# Revit family: Hager-Golf-IP40-Transparent_Door-sistema-NoHosted-IT-it
name_source: partatom
category: Electrical Equipment
units: mm (PartAtom-declared; Revit-internal decimal feet)

## family parameters
Always vertical = Yes
Cut with Voids When Loaded = No
Panel Configuration = Two Columns, Circuits Across
Part Type = Panelboard
Room Calculation Point = No
Round Connector Dimension = Use Diameter
Shared = No
Work Plane-Based = Yes

## types (22) — shared parameters
Default Elevation = 1219 mm
EF000007 - colore = EV000202 - bianco
EF000116 - numero RAL = 9010
EF000118 - con piastra di montaggio = No
EF000339 - tipo di copertura = EV004216 - porta
EF001062 - esecuzione EMC = No
EF001088 - possibilità di applicazione = Yes
EF001134 - barra DIN = Yes
EF001596 - Attacco Lampada = EV000139 - plastica
EF004462 - tipo di chiusura = EV000154 - altri
EF006244 - coperchio/porta trasparente = Yes
EF006306 - con serratura = No
EF009212 - esecuzione coperchio = EV000116 - chiuso
EF015776 - Morsettiera di terra = No
EF015777 - Morsettiera neutra = No
EF015941 - Segnale di passaggio porta = Yes
HG000001 - Numero di colonne = 1
HG000002 - Con porta = Yes
HG000003 - Gamma = Golf
HG000005 - Spessore = 3 mm  [stored 0.00984252 ft]
HG000009 - Porta doppia a battente = No
HG000010 - Porte asimmetriche = No
HG000011 - File vuote nella parte basse = No
HG000017 - Distanza tra i poli = 18 mm  [stored 0.0590551 ft]
Manufacturer = Hager
Type Comments = Golf
zero-valued in all types: HG000007 - Numero di colonne vuote, HG000008 - Numero di file vuote

## per-type parameters (varying)
| type | EF000003 - Tipo di montaggio | EF000008 - Larghezza | EF000040 - Altezza | EF000049 - profondità | EF000218 - profondità di incasso | EF000266 - numero di file | EF000332 - Altezza della parte incassata | EF000846 - larghezza di montaggio | EF001131 - profondità interna | EF002950 - Numero moduli DIN | EF005474 - grado di protezione (IP) | HG000004 - Codice produttore | HG000006 - Ad incasso | Model |
| A parete  L138 A184 P99 4 Unità di divisione - VS104TG | EV000384 - A parete | 138 mm  [stored 0.452756 ft] | 184 mm  [stored 0.603675 ft] | 99 mm  [stored 0.324803 ft] | 0 mm  [stored 0 ft] | 1 | 0 mm  [stored 0 ft] | 0 mm  [stored 0 ft] | 99 mm  [stored 0.324803 ft] | 4 |  | VS104TG | No | VS104TG |
| A parete  L210 A184 P99 8 Unità di divisione - VS108TG | EV000384 - A parete | 210 mm  [stored 0.688976 ft] | 184 mm  [stored 0.603675 ft] | 99 mm  [stored 0.324803 ft] | 0 mm  [stored 0 ft] | 1 | 0 mm  [stored 0 ft] | 0 mm  [stored 0 ft] | 99 mm  [stored 0.324803 ft] | 8 |  | VS108TG | No | VS108TG |
| A parete IP40 L282 A252 P99 12 Unità di divisione - VS112TG | EV000384 - A parete | 282 mm | 252 mm  [stored 0.826772 ft] | 99 mm  [stored 0.324803 ft] | 0 mm  [stored 0 ft] | 1 | 0 mm  [stored 0 ft] | 0 mm  [stored 0 ft] | 99 mm  [stored 0.324803 ft] | 12 | EV006415 - IP40 | VS112TG | No | VS112TG |
| A parete IP40 L282 A377 P99 12 Unità di divisione - VS212TG | EV000384 - A parete | 282 mm | 377 mm  [stored 1.23688 ft] | 99 mm  [stored 0.324803 ft] | 0 mm  [stored 0 ft] | 2 | 0 mm  [stored 0 ft] | 0 mm  [stored 0 ft] | 99 mm  [stored 0.324803 ft] | 12 | EV006415 - IP40 | VS212TG | No | VS212TG |
| A parete IP40 L282 A500 P99 12 Unità di divisione - VS312TG | EV000384 - A parete | 282 mm | 500 mm  [stored 1.64042 ft] | 99 mm  [stored 0.324803 ft] | 0 mm  [stored 0 ft] | 3 | 0 mm  [stored 0 ft] | 0 mm  [stored 0 ft] | 99 mm  [stored 0.324803 ft] | 12 | EV006415 - IP40 | VS312TG | No | VS312TG |
| A parete IP40 L282 A647 P99 12 Unità di divisione - VS412TG | EV000384 - A parete | 282 mm | 647 mm  [stored 2.1227 ft] | 99 mm  [stored 0.324803 ft] | 0 mm  [stored 0 ft] | 4 | 0 mm  [stored 0 ft] | 0 mm  [stored 0 ft] | 99 mm  [stored 0.324803 ft] | 12 | EV006415 - IP40 | VS412TG | No | VS412TG |
| A parete IP40 L390 A252 P99 18 Unità di divisione - VS118TG | EV000384 - A parete | 390 mm  [stored 1.27953 ft] | 252 mm  [stored 0.826772 ft] | 99 mm  [stored 0.324803 ft] | 0 mm  [stored 0 ft] | 1 | 0 mm  [stored 0 ft] | 0 mm  [stored 0 ft] | 99 mm  [stored 0.324803 ft] | 18 | EV006415 - IP40 | VS118TG | No | VS118TG |
| A parete IP40 L390 A377 P99 18 Unità di divisione - VS218TG | EV000384 - A parete | 390 mm  [stored 1.27953 ft] | 377 mm  [stored 1.23688 ft] | 99 mm  [stored 0.324803 ft] | 0 mm  [stored 0 ft] | 2 | 0 mm  [stored 0 ft] | 0 mm  [stored 0 ft] | 99 mm  [stored 0.324803 ft] | 18 | EV006415 - IP40 | VS218TG | No | VS218TG |
| A parete IP40 L390 A500 P99 18 Unità di divisione - VS318TG | EV000384 - A parete | 390 mm  [stored 1.27953 ft] | 500 mm  [stored 1.64042 ft] | 99 mm  [stored 0.324803 ft] | 0 mm  [stored 0 ft] | 3 | 0 mm  [stored 0 ft] | 0 mm  [stored 0 ft] | 99 mm  [stored 0.324803 ft] | 18 | EV006415 - IP40 | VS318TG | No | VS318TG |
| A parete IP40 L390 A647 P99 18 Unità di divisione - VS418TG | EV000384 - A parete | 390 mm  [stored 1.27953 ft] | 647 mm  [stored 2.1227 ft] | 99 mm  [stored 0.324803 ft] | 0 mm  [stored 0 ft] | 4 | 0 mm  [stored 0 ft] | 0 mm  [stored 0 ft] | 99 mm  [stored 0.324803 ft] | 18 | EV006415 - IP40 | VS418TG | No | VS418TG |
| A parete IP40 L462 A252 P99 22 Unità di divisione - VS122TG | EV000384 - A parete | 462 mm  [stored 1.51575 ft] | 252 mm  [stored 0.826772 ft] | 99 mm  [stored 0.324803 ft] | 0 mm  [stored 0 ft] | 1 | 0 mm  [stored 0 ft] | 0 mm  [stored 0 ft] | 99 mm  [stored 0.324803 ft] | 22 | EV006415 - IP40 | VS122TG | No | VS122TG |
| incassato  L204 A225 P97.5 4 Unità di divisione - VF104TG | EV000383 - incassato | 204 mm | 225 mm  [stored 0.738189 ft] | 98 mm  [stored 0.321522 ft] | 72 mm  [stored 0.23622 ft] | 1 | 189 mm  [stored 0.620079 ft] | 170 mm  [stored 0.557743 ft] | 98 mm  [stored 0.321522 ft] | 4 |  | VF104TG | Yes | VF104TG |
| incassato  L275 A225 P97.5 8 Unità di divisione - VF108TG | EV000383 - incassato | 275 mm | 225 mm  [stored 0.738189 ft] | 98 mm  [stored 0.321522 ft] | 72 mm  [stored 0.23622 ft] | 1 | 189 mm  [stored 0.620079 ft] | 242 mm  [stored 0.793963 ft] | 98 mm  [stored 0.321522 ft] | 8 |  | VF108TG | Yes | VF108TG |
| incassato IP40 L352 A293 P97.5 12 Unità di divisione - VF112TG | EV000383 - incassato | 352 mm  [stored 1.15486 ft] | 293 mm | 98 mm  [stored 0.321522 ft] | 72 mm  [stored 0.23622 ft] | 1 | 257 mm  [stored 0.843176 ft] | 318 mm  [stored 1.04331 ft] | 98 mm  [stored 0.321522 ft] | 12 | EV006415 - IP40 | VF112TG | Yes | VF112TG |
| incassato IP40 L352 A543 P97.5 12 Unità di divisione - VF312TG | EV000383 - incassato | 352 mm  [stored 1.15486 ft] | 543 mm  [stored 1.7815 ft] | 98 mm  [stored 0.321522 ft] | 72 mm  [stored 0.23622 ft] | 3 | 507 mm  [stored 1.66339 ft] | 318 mm  [stored 1.04331 ft] | 98 mm  [stored 0.321522 ft] | 12 | EV006415 - IP40 | VF312TG | Yes | VF312TG |
| incassato IP40 L352 A688 P97.5 12 Unità di divisione - VF412TG | EV000383 - incassato | 352 mm  [stored 1.15486 ft] | 688 mm  [stored 2.25722 ft] | 98 mm  [stored 0.321522 ft] | 72 mm  [stored 0.23622 ft] | 4 | 652 mm  [stored 2.13911 ft] | 318 mm  [stored 1.04331 ft] | 98 mm  [stored 0.321522 ft] | 12 | EV006415 - IP40 | VF412TG | Yes | VF412TG |
| incassato IP40 L382 A418 P97.5 12 Unità di divisione - VF212TG | EV000383 - incassato | 382 mm  [stored 1.25328 ft] | 418 mm  [stored 1.37139 ft] | 98 mm  [stored 0.321522 ft] | 72 mm  [stored 0.23622 ft] | 2 | 382 mm  [stored 1.25328 ft] | 318 mm  [stored 1.04331 ft] | 98 mm  [stored 0.321522 ft] | 12 | EV006415 - IP40 | VF212TG | Yes | VF212TG |
| incassato IP40 L460 A293 P97.5 18 Unità di divisione - VF118TG | EV000383 - incassato | 460 mm  [stored 1.50919 ft] | 293 mm | 98 mm  [stored 0.321522 ft] | 72 mm  [stored 0.23622 ft] | 1 | 257 mm  [stored 0.843176 ft] | 426 mm  [stored 1.39764 ft] | 98 mm  [stored 0.321522 ft] | 18 | EV006415 - IP40 | VF118TG | Yes | VF118TG |
| incassato IP40 L460 A418 P97.5 18 Unità di divisione - VF218TG | EV000383 - incassato | 460 mm  [stored 1.50919 ft] | 418 mm  [stored 1.37139 ft] | 98 mm  [stored 0.321522 ft] | 72 mm  [stored 0.23622 ft] | 2 | 382 mm  [stored 1.25328 ft] | 426 mm  [stored 1.39764 ft] | 98 mm  [stored 0.321522 ft] | 18 | EV006415 - IP40 | VF218TG | Yes | VF218TG |
| incassato IP40 L460 A543 P97.5 18 Unità di divisione - VF318TG | EV000383 - incassato | 460 mm  [stored 1.50919 ft] | 543 mm  [stored 1.7815 ft] | 98 mm  [stored 0.321522 ft] | 72 mm  [stored 0.23622 ft] | 3 | 507 mm  [stored 1.66339 ft] | 426 mm  [stored 1.39764 ft] | 98 mm  [stored 0.321522 ft] | 18 | EV006415 - IP40 | VF318TG | Yes | VF318TG |
| incassato IP40 L460 A688 P97.5 18 Unità di divisione - VF418TG | EV000383 - incassato | 460 mm  [stored 1.50919 ft] | 688 mm  [stored 2.25722 ft] | 98 mm  [stored 0.321522 ft] | 72 mm  [stored 0.23622 ft] | 4 | 652 mm  [stored 2.13911 ft] | 426 mm  [stored 1.39764 ft] | 98 mm  [stored 0.321522 ft] | 18 | EV006415 - IP40 | VF418TG | Yes | VF418TG |
| incassato IP40 L532 A293 P97.5 22 Unità di divisione - VF122TG | EV000383 - incassato | 532 mm  [stored 1.74541 ft] | 293 mm | 98 mm  [stored 0.321522 ft] | 72 mm  [stored 0.23622 ft] | 1 | 257 mm  [stored 0.843176 ft] | 498 mm  [stored 1.63386 ft] | 98 mm  [stored 0.321522 ft] | 22 | EV006415 - IP40 | VF122TG | Yes | VF122TG |

note: [stored X ft] marks values corroborated as IEEE doubles in the binary element streams (Revit-internal decimal feet)

## geometry (parser evidence)
native form markers: Sweep x13
no freeform markers — native parametric forms only
